# Revit family: LSVA24
name_source: partatom
category: Lighting Fixtures
units: mm (PartAtom-declared; Revit-internal decimal feet)

## family parameters
Always vertical = Yes
Cut with Voids When Loaded = No
Host = Ceiling
Light Source = Yes
OmniClass Number = 23.80.70.11
OmniClass Title = Luminaries for Internal Lighting
Part Type = Normal
Room Calculation Point = No
Round Connector Dimension = Use Diameter
Shared = No

## types (2) — shared parameters
Assembly Code = D5020200
Color Filter = 16777215
Description = LED Sealed Vapour A
Dimming Lamp Color Temperature Shift = <None>
Emit from Line Length = 2' - 1 13/16"
Housing Finish = Metal - Viscor - White
Lamp = LED
Length = 2' - 1 13/16"
Lens Finsih = Acrylic - Viscor - High Impact Textured
Manufacturer = VISIONEERING by VISCOR
Model = LSVA24
Tilt Angle = 90.00°
URL = https://www.viscor.com
Voltage = 120 V
Width = 0' - 7"

## per-type parameters (varying)
| type | Apparent Load | Lamp Wattage | Photometric Web File |
| LSVA24-LED840K022LUNV-P15 | 15 VA | 15 VA | LSVA24-LED840K022LUNV-P15.ies |
| LSVA24-LED840K042LUNV-P15 | 30 VA | 30 VA | LSVA24-LED840K042LUNV-P15.ies |

## geometry (parser evidence)
native form markers: Sweep x3
no freeform markers — native parametric forms only
